# Revit family: IS_iLifeA_T4674_BIM_NL
name_source: partatom
category: Plumbing Fixtures
units: mm (PartAtom-declared; Revit-internal decimal feet)

## family parameters
Always vertical = No
Cut with Voids When Loaded = No
OmniClass Number = 23.45.05.14.27
OmniClass Title = Bidets
Part Type = Normal
Room Calculation Point = No
Round Connector Dimension = Use Diameter
Shared = No
Work Plane-Based = No

## types (1)
- T467401 - I.life A single bidet white - White
    Accesoires = https://www.idealstandard.nl
    Accessories = https://www.idealstandard.nl
    Afmetingen = 485 x 400 x 360mm
    AfstandsEenheid = millimeter
    Afwerking = Weiß
    AreaMeasurement = internal
    AreaUnits = Millimeter
    Artikelnummer = T467401
    Artikelomschrijving = I.life Ein einzelnes Bidet weiß - Weiß
    Artikelreferentie = I.life Ein einzelnes Bidet weiß
    Auteur = Ideal Standard
    BIMObjectName = IS_IdealStandard_Bidets__I.life__T4674
    BIMobject category = Bidets
    BIMobject category code = sanitary-bidets
    BIMobject main category = Sanitary
    BIMobject main category code = sanitary
    BarCode = 8014140486077
    Barcode = 8014140486077
    Beschrijvinggarantie = Herstellergarantie
    BidetMounting = Floor Standing
    BimObjectNaam = IS_IdealStandard_Bidets__I.life__T4674
    Brand = Ideal Standard
    Brand url = http://https:
    Breedte = 0
    BrutoGewicht = 0
    Color = Weiß
    ConnectionType = Plumbing
    Cost = 0 $
    CurrencyUnit = €
    CurrentRevision = 1
    Date of publishing = 28/06/2021
    Description = I.life Ein einzelnes Bidet weiß - Weiß
    Diepte = 0 mm  [stored 0 ft]
    DrainSize = 0 mm  [stored 0 ft]
    DurationUnit = Years
    DuurEenheid = Jaar
    Edition number = 1
    Eigenschappen = Einzel-Bidet weiß
    Features = Single bidet white
    Finish = Weiß
    GTIN code = https://8014140486077
    Garantieonderdelen = 5
    Garantieunits = Jaar
    GemaaktOp = 40722
    GrootteAfvoergat = 0
    Help = https://www.idealstandard.nl
    Hoogte = 400.08326568909
    Hulp = https://www.idealstandard.nl
    IFC Classification = Sanitary Terminal
    IfcExportAs = IfcSanitaryTerminalType
    IfcExportType = BIDET
    Installatieinstructies = https://www.idealstandard.nl
    Installation instructions = https://www.idealstandard.nl
    InstallationInstructions = https://www.idealstandard.nl
    Kleur = Weiß
    Lengte = 485 mm
    LinearUnits = millimeter
    MainColor = White
    MaintenanceInformation = https://www.idealstandard.nl
    Manufacturer = Ideal Standard
    Manufacturer name = Ideal Standard
    ManufacturerURL = https://www.idealstandard.nl
    Masterformat 2014 Code = 22 41 13.19
    Masterformat 2014 Description = Residential Bidets
    Materiaal = Vitrous China
    Material = Vitrous China
    Material main = Vitrous China
    Merk = Ideal Standard
    Model = T467401
    ModelNumber = T467401
    ModelReference = I.life A single bidet white
    Montageinstuctie = https://www.idealstandard.nl
    NBS Reference Code = 35-06-11
    NBS Reference Description = Bidets
    Name = Bidets__I.life__T4674_IdealStandard
    NettWeight = 16.45
    Nettogewicht = 16.45
    NominalDepth = 485 mm
    NominalHeight = 400 mm
    NominalWidth = 360 mm
    Normen = Bidets__I.life__T4674_IdealStandard
    OmniClass Code = 23-31 23 00
    OmniClass Description = Bidets
    OppervlakteEenheid = Millimeter
    Overloop = 0 mm  [stored 0 ft]
    Product Guid = a5ebcacd-bac5-4c66-b189-53e7a0c45f61
    Product SKU = T4674
    Product certification = https://www.idealstandard.nl
    Product data url = https://bimobject.com
    Product family = I.life
    Product group = Bidet
    Product name = I.life A single bidet white
    Product url = https://www.idealstandard.nl
    ProductInformation = https://www.idealstandard.nl
    ProductSoort = Bidets
    Productinformatie = https://www.idealstandard.nl
    QR code = http://bimobject.com
    Referentie = I.life Ein einzelnes Bidet weiß
    Revisie = 1
    Shape = sculpture
    Size = 485 x 400 x 360mm
    Space = Internal
    SpareParts = https://www.idealstandard.nl
    Technical description = https://www.idealstandard.nl
    Telefoonnummer = 077 355 08 08
    Typeconnectie = Installation
    UNSPSC Code = 30181502
    URL = https://https:
    Uniclass 1.4 Code = L7215
    Uniclass 1.4 Description = Bidets
    Uniclass 2.0 Code = PR-35-06-11
    Uniclass 2.0 Description = Bidets
    Uniclass 2015 Code = Pr_40_20_06_11
    Uniclass 2015 Name = Bidets
    Uniclass2015Beschrijving = Bidets
    Uniclass2015Code = Pr_40_20_06_11
    Uniclass2015Referentie = Pr_40_20_06_11
    Uniclass2015Title = Bidets
    Uniclass2015Version = v1.20
    Urlproducent = https://https:
    ValutaEenheid = €
    Versie = 1
    Version = 1
    Vervangingskosten = 0
    VolumeUnits = Liter
    Volumeunits = Liter
    Vorm = beeldhouwwerk
    WRASURL = https://www.wrasapprovals.co.uk
    WarrantyDescription = manufacturer warranty
    WarrantyDurationParts = 99
    WarrantyDurationUnit = years
    Wisselstukken = https://www.idealstandard.nl
    Youtube clip = https://www.youtube.com

note: [stored X ft] marks values corroborated as IEEE doubles in the binary element streams (Revit-internal decimal feet)

## geometry (parser evidence)
native form markers: Sweep x3
no freeform markers — native parametric forms only
